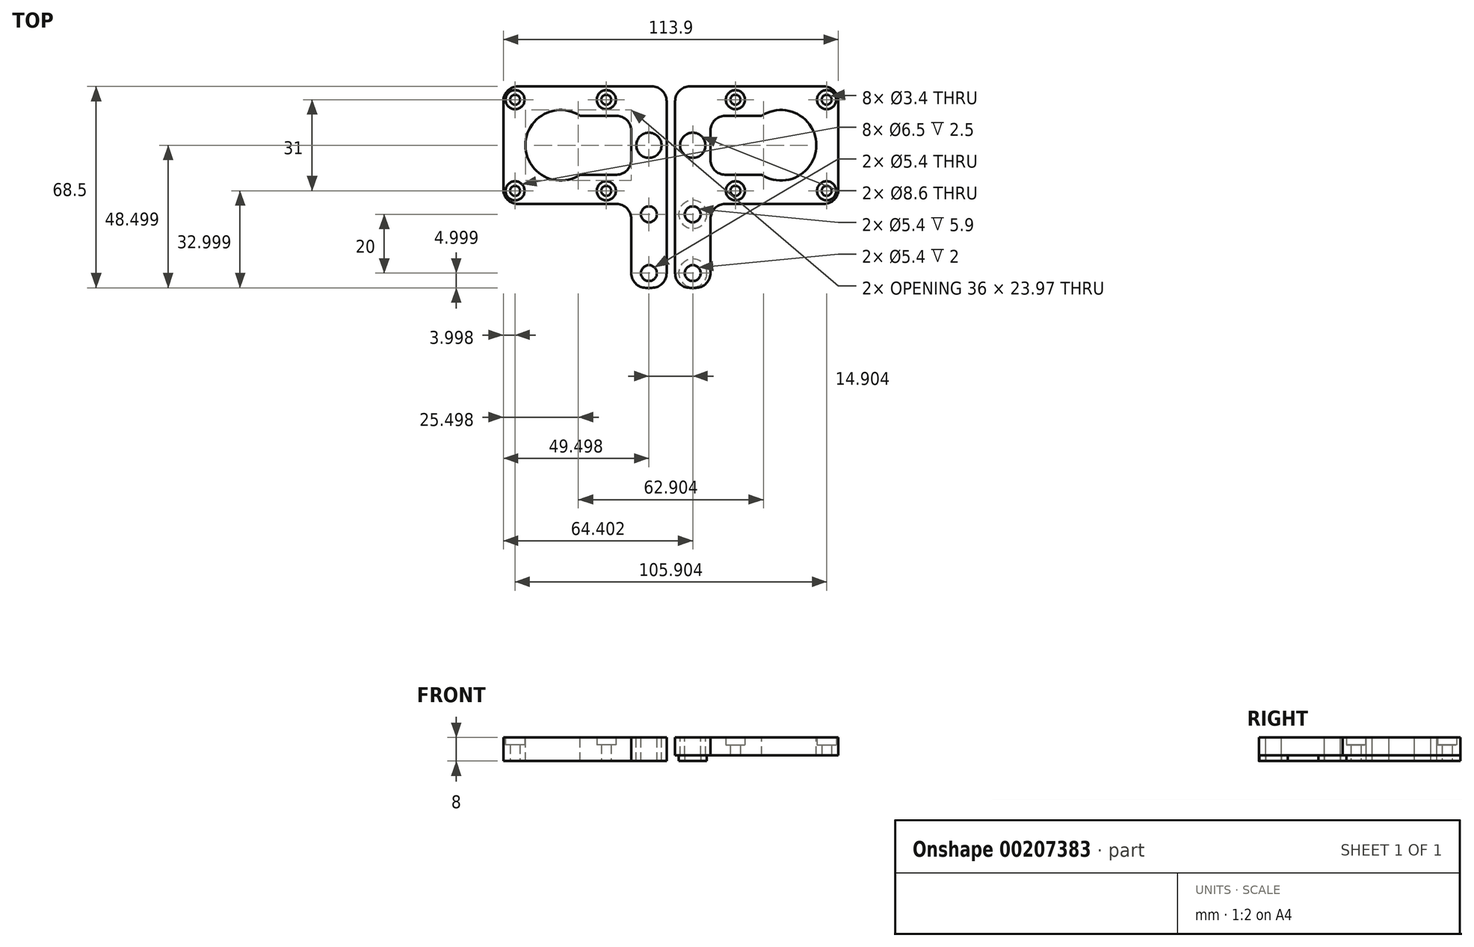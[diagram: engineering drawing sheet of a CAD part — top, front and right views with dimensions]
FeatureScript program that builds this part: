
annotation { "Feature Type Name" : "Feature", "Feature Type Description" : "" }
export const myFeature = defineFeature(function(context is Context, id is Id, definition is map)
    precondition{}
    {
        {
            var Q0;
            Q0=qCreatedBy(makeId("Top.planeOp"),FACE);
            var sketch = newSketch(context, id + "F0", { "sketchPlane" : qUnion([Q0])});
            skLineSegment(sketch, "E0.top", {"start": v(1.45, 0.9) * mm, "end": v(13.45, 0.9) * mm});
            skCircle(sketch, "E1", {"center": v(7.45, 49.4) * mm, "radius": 4.3 * mm});
            skCircle(sketch, "E2", {"center": v(7.45, 25.9) * mm, "radius": 2.7 * mm});
            skCircle(sketch, "E3", {"center": v(7.45, 5.9) * mm, "radius": 2.7 * mm});
            skPoint(sketch, "E4", {"position": v(7.45, 0.9) * mm});
            skLineSegment(sketch, "E5", {"start": v(56.95, 29.4) * mm, "end": v(56.95, 69.4) * mm});
            skLineSegment(sketch, "E6", {"start": v(13.45, 59.4) * mm, "end": v(48.95, 59.4) * mm});
            skLineSegment(sketch, "E7", {"start": v(21.95, 33.9) * mm, "end": v(52.95, 64.9) * mm, "construction": true});
            skLineSegment(sketch, "E8", {"start": v(52.95, 33.9) * mm, "end": v(21.95, 64.9) * mm, "construction": true});
            skPoint(sketch, "E9", {"position": v(37.45, 49.4) * mm});
            skLineSegment(sketch, "E10", {"start": v(13.45, 29.4) * mm, "end": v(56.95, 29.4) * mm});
            skLineSegment(sketch, "E11", {"start": v(13.45, 69.4) * mm, "end": v(56.95, 69.4) * mm});
            skLineSegment(sketch, "E12", {"start": v(13.45, 69.4) * mm, "end": v(1.45, 69.4) * mm});
            skLineSegment(sketch, "E13", {"start": v(48.95, 59.4) * mm, "end": v(48.95, 39.4) * mm});
            skLineSegment(sketch, "E14", {"start": v(48.95, 39.4) * mm, "end": v(13.45, 39.4) * mm});
            skLineSegment(sketch, "E15", {"start": v(13.45, 0.9) * mm, "end": v(13.45, 29.4) * mm});
            skLineSegment(sketch, "E16", {"start": v(1.45, 0.9) * mm, "end": v(1.45, 69.4) * mm});
            skLineSegment(sketch, "E17", {"start": v(13.45, 39.4) * mm, "end": v(13.45, 59.4) * mm});
            skCircle(sketch, "E18", {"center": v(37.45, 49.4) * mm, "radius": 12 * mm});
            skCircle(sketch, "E19", {"center": v(7.45, 5.9) * mm, "radius": 4.8 * mm});
            skCircle(sketch, "E20", {"center": v(7.45, 25.9) * mm, "radius": 4.8 * mm});
            skSolve(sketch);
        }
        {
            var Q0;
            Q0=makeQuery(id+"F0.imprint","IMPRINT",FACE,{"disambiguationData":[TD([[makeQuery(id+"F0.imprint","IMPRINT",EDGE,{"derivedFrom":sQuery(id+"F0.wireOp",EDGE,"E0.bottom")}),-1.0]])]});
            var Q1;
            {var subQ1=sQuery(id+"F0.wireOp",EDGE,"d5d79a18-1b9a-439a-83fc-479bf9618a3d");Q1=makeQuery(id+"F0.imprint","IMPRINT",FACE,{"disambiguationData":[TD([[makeQuery(id+"F0.imprint","IMPRINT",EDGE,{"derivedFrom":subQ1}),-1.0]])]});}
            var Q2;
            Q2=makeQuery(id+"F0.imprint","IMPRINT",FACE,{"disambiguationData":[TD([[makeQuery(id+"F0.imprint","IMPRINT",EDGE,{"derivedFrom":sQuery(id+"F0.wireOp",EDGE,"E0.bottom")}),1.0]])]});
            var Q3;
            {var subQ5=sQuery(id+"F0.wireOp",EDGE,"E0.top");Q3=makeQuery(id+"F0.imprint","IMPRINT",FACE,{"disambiguationData":[TD([[makeQuery(id+"F0.imprint","IMPRINT",EDGE,{"derivedFrom":subQ5}),1.0]])]});}
            var Q4;
            {var subQ4=sQuery(id+"F0.wireOp",EDGE,"c570f75a-df84-4235-972a-370a758feee2");Q4=makeQuery(id+"F0.imprint","IMPRINT",FACE,{"disambiguationData":[TD([[makeQuery(id+"F0.imprint","IMPRINT",EDGE,{"derivedFrom":subQ4}),-1.0]])]});}
            var Q5;
            Q5=makeQuery(id+"F0.imprint","IMPRINT",FACE,{"disambiguationData":[TD([[makeQuery(id+"F0.imprint","IMPRINT",EDGE,{"derivedFrom":sQuery(id+"F0.wireOp",EDGE,"E5")}),1.0]])]});
            var Q6;
            {var subQ0=sQuery(id+"F0.wireOp",EDGE,"E13");var subQ1=sQuery(id+"F0.wireOp",EDGE,"E6");var subQ2=makeQuery(id+"F0.imprint","INTERSECT",VERTEX,{"derivedFrom":[subQ1,subQ0]});Q6=makeQuery(id+"F0.imprint","IMPRINT",FACE,{"disambiguationData":[TD([[makeQuery(id+"F0.imprint","IMPRINT",EDGE,{"disambiguationData":[TD([[subQ2,1.0]])],"derivedFrom":subQ1}),-1.0]])]});}
            var Q7;
            {var subQ0=sQuery(id+"F0.wireOp",EDGE,"E14");var subQ1=sQuery(id+"F0.wireOp",EDGE,"E13");var subQ2=makeQuery(id+"F0.imprint","INTERSECT",VERTEX,{"derivedFrom":[subQ1,subQ0]});Q7=makeQuery(id+"F0.imprint","IMPRINT",FACE,{"disambiguationData":[TD([[makeQuery(id+"F0.imprint","IMPRINT",EDGE,{"disambiguationData":[TD([[subQ2,1.0]])],"derivedFrom":subQ1}),-1.0]])]});}
            var Q8;
            Q8=makeQuery(id+"F0.imprint","IMPRINT",FACE,{"disambiguationData":[TD([[makeQuery(id+"F0.imprint","IMPRINT",EDGE,{"derivedFrom":sQuery(id+"F0.wireOp",EDGE,"E3")}),-1.0]])]});
            var Q9;
            Q9=makeQuery(id+"F0.imprint","IMPRINT",FACE,{"disambiguationData":[TD([[makeQuery(id+"F0.imprint","IMPRINT",EDGE,{"derivedFrom":sQuery(id+"F0.wireOp",EDGE,"E2")}),-1.0]])]});
            extrude(context, id + "F1", {"entities" : qUnion([Q0, Q1, Q2, Q3, Q4, Q5, Q6, Q7, Q8, Q9]), "oppositeDirection" : true, "depth" : 8 * mm, "offsetDistance" : 25 * mm});
        }
        {
            var Q0;
            Q0=makeQuery(id+"F1.opExtrude","SWEPT_EDGE",EDGE,{"disambiguationData":[OSD([sQuery(id+"F0.wireOp",EDGE,"E5"),sQuery(id+"F0.wireOp",EDGE,"E10")])]});
            var Q1;
            Q1=makeQuery(id+"F1.opExtrude","SWEPT_EDGE",EDGE,{"disambiguationData":[OSD([sQuery(id+"F0.wireOp",EDGE,"E5"),sQuery(id+"F0.wireOp",EDGE,"E11")])]});
            var Q2;
            Q2=makeQuery(id+"F1.opExtrude","SWEPT_EDGE",EDGE,{"disambiguationData":[OSD([sQuery(id+"F0.wireOp",EDGE,"E12"),sQuery(id+"F0.wireOp",EDGE,"E16")])]});
            var Q3;
            Q3=makeQuery(id+"F1.opExtrude","SWEPT_EDGE",EDGE,{"disambiguationData":[OSD([sQuery(id+"F0.wireOp",EDGE,"E0.top"),sQuery(id+"F0.wireOp",EDGE,"E15")])]});
            var Q4;
            Q4=makeQuery(id+"F1.opExtrude","SWEPT_EDGE",EDGE,{"disambiguationData":[OSD([sQuery(id+"F0.wireOp",EDGE,"E0.top"),sQuery(id+"F0.wireOp",EDGE,"E16")])]});
            var Q5;
            Q5=makeQuery(id+"F1.opExtrude","SWEPT_EDGE",EDGE,{"disambiguationData":[OSD([sQuery(id+"F0.wireOp",EDGE,"E10"),sQuery(id+"F0.wireOp",EDGE,"E15")])]});
            var Q6;
            Q6=makeQuery(id+"F1.opExtrude","SWEPT_EDGE",EDGE,{"disambiguationData":[OSD([sQuery(id+"F0.wireOp",EDGE,"E6"),sQuery(id+"F0.wireOp",EDGE,"E17")])]});
            var Q7;
            Q7=makeQuery(id+"F1.opExtrude","SWEPT_EDGE",EDGE,{"disambiguationData":[OSD([sQuery(id+"F0.wireOp",EDGE,"E14"),sQuery(id+"F0.wireOp",EDGE,"E17")])]});
            fillet(context, id + "F2", {"entities" : qUnion([Q0, Q1, Q2, Q3, Q4, Q5, Q6, Q7]), "radius" : 5 * mm, "tangentPropagation" : true, "allowEdgeOverflow" : false});
        }
        {
            var Q0;
            Q0=sQuery(id+"F0.wireOp",VERTEX,"E8.end");
            var Q1;
            Q1=sQuery(id+"F0.wireOp",VERTEX,"E7.end");
            var Q2;
            Q2=sQuery(id+"F0.wireOp",VERTEX,"E8.start");
            var Q3;
            Q3=sQuery(id+"F0.wireOp",VERTEX,"E7.start");
            var Q4;
            Q4=makeQuery(id+"F1.opExtrude","SWEPT_BODY",BODY,{"disambiguationData":[OSD([sQuery(id+"F0.wireOp",EDGE,"E0.top"),sQuery(id+"F0.wireOp",EDGE,"E1"),sQuery(id+"F0.wireOp",EDGE,"E2"),sQuery(id+"F0.wireOp",EDGE,"E3"),sQuery(id+"F0.wireOp",EDGE,"E5"),sQuery(id+"F0.wireOp",EDGE,"E6"),sQuery(id+"F0.wireOp",EDGE,"E10"),sQuery(id+"F0.wireOp",EDGE,"E11"),sQuery(id+"F0.wireOp",EDGE,"E12"),sQuery(id+"F0.wireOp",EDGE,"E14"),sQuery(id+"F0.wireOp",EDGE,"E15"),sQuery(id+"F0.wireOp",EDGE,"E16"),sQuery(id+"F0.wireOp",EDGE,"E17"),sQuery(id+"F0.wireOp",EDGE,"E18")])]});
            hole(context, id + "F3", {"style" : HoleStyle.C_BORE, "endStyle" : HoleEndStyle.THROUGH, "holeDiameter" : 3.4 * mm, "cBoreDiameter" : 6.5 * mm, "cBoreDepth" : 2.5 * mm, "majorDiameter" : 5 * mm, "isTappedThrough" : true, "tappedDepth" : 12 * mm, "tapClearance" : 3, "locations" : qUnion([Q0, Q1, Q2, Q3]), "scope" : qUnion([Q4]), "startStyle" : HoleStartStyle.PART});
        }
        {
            var Q0;
            Q0=makeQuery(id+"F1.opExtrude","SWEPT_BODY",BODY,{"disambiguationData":[OSD([sQuery(id+"F0.wireOp",EDGE,"E0.top"),sQuery(id+"F0.wireOp",EDGE,"E0.left"),sQuery(id+"F0.wireOp",EDGE,"E0.right"),sQuery(id+"F0.wireOp",EDGE,"E1"),sQuery(id+"F0.wireOp",EDGE,"E2"),sQuery(id+"F0.wireOp",EDGE,"E3"),sQuery(id+"F0.wireOp",EDGE,"d5d79a18-1b9a-439a-83fc-479bf9618a3d"),sQuery(id+"F0.wireOp",EDGE,"c570f75a-df84-4235-972a-370a758feee2"),sQuery(id+"F0.wireOp",EDGE,"a2be1d45-0dba-40e6-a96d-5c1e5a46a9f0"),sQuery(id+"F0.wireOp",EDGE,"d066aa0a-05fd-4a1e-85b8-d3e250bc6735"),sQuery(id+"F0.wireOp",EDGE,"028c346d-4075-4f4f-a344-9214535dc93d"),sQuery(id+"F0.wireOp",EDGE,"923343ab-d8ea-4514-8808-893b9cc318f7"),sQuery(id+"F0.wireOp",EDGE,"97896662-81bd-4ab9-9ddb-92a6698ae74e"),sQuery(id+"F0.wireOp",EDGE,"62df8057-97cc-498b-857e-02ef16877537")])]});
            var Q1;
            Q1=qCreatedBy(makeId("Right.planeOp"),FACE);
            mirror(context, id + "F4", {"entities" : qUnion([Q0]), "mirrorPlane" : qUnion([Q1])});
        }
        {
            var Q0;
            Q0=makeQuery(id+"F1.opExtrude","CAP_FACE",FACE,{"disambiguationData":[OSD([sQuery(id+"F0.wireOp",EDGE,"E0.top"),sQuery(id+"F0.wireOp",EDGE,"E1"),sQuery(id+"F0.wireOp",EDGE,"E2"),sQuery(id+"F0.wireOp",EDGE,"E3"),sQuery(id+"F0.wireOp",EDGE,"E5"),sQuery(id+"F0.wireOp",EDGE,"E6"),sQuery(id+"F0.wireOp",EDGE,"E10"),sQuery(id+"F0.wireOp",EDGE,"E11"),sQuery(id+"F0.wireOp",EDGE,"E12"),sQuery(id+"F0.wireOp",EDGE,"E14"),sQuery(id+"F0.wireOp",EDGE,"E15"),sQuery(id+"F0.wireOp",EDGE,"E16"),sQuery(id+"F0.wireOp",EDGE,"E17"),sQuery(id+"F0.wireOp",EDGE,"E18")])],"isStart":false});
            var sketch = newSketch(context, id + "F5", { "sketchPlane" : qUnion([Q0])});
            skCircle(sketch, "E21.0", {"center": v(7.45, -5.9) * mm, "radius": 4.8 * mm});
            skCircle(sketch, "E22.0", {"center": v(7.45, -25.9) * mm, "radius": 4.8 * mm});
            skCircle(sketch, "E23.0", {"center": v(7.45, -5.9) * mm, "radius": 2.7 * mm});
            skSolve(sketch);
        }
        {
            var Q0;
            Q0=makeQuery(id+"F5.imprint","IMPRINT",FACE,{"disambiguationData":[TD([[makeQuery(id+"F5.imprint","IMPRINT",EDGE,{"derivedFrom":sQuery(id+"F5.wireOp",EDGE,"E21.0")}),-1.0]])]});
            var Q1;
            Q1=makeQuery(id+"F5.imprint","IMPRINT",FACE,{"disambiguationData":[TD([[makeQuery(id+"F5.imprint","IMPRINT",EDGE,{"derivedFrom":sQuery(id+"F5.wireOp",EDGE,"E23.0")}),-1.0]])]});
            var Q2;
            Q2=makeQuery(id+"F5.imprint","IMPRINT",FACE,{"disambiguationData":[TD([[makeQuery(id+"F5.imprint","IMPRINT",EDGE,{"derivedFrom":makeQuery(id+"F1.opExtrude","CAP_EDGE",EDGE,{"disambiguationData":[OSD([sQuery(id+"F0.wireOp",EDGE,"E2")])],"isStart":false})}),-1.0]])]});
            extrude(context, id + "F6", {"entities" : qUnion([Q0, Q1, Q2]), "operationType" : NewBodyOperationType.ADD, "oppositeDirection" : true, "depth" : 2.1 * mm, "offsetDistance" : 25 * mm});
        }
        {
            var Q0;
            Q0=makeQuery(id+"F5.imprint","IMPRINT",FACE,{"disambiguationData":[TD([[makeQuery(id+"F5.imprint","IMPRINT",EDGE,{"derivedFrom":sQuery(id+"F5.wireOp",EDGE,"E21.0")}),-1.0]])]});
            var Q1;
            Q1=makeQuery(id+"F5.imprint","IMPRINT",FACE,{"disambiguationData":[TD([[makeQuery(id+"F5.imprint","IMPRINT",EDGE,{"derivedFrom":sQuery(id+"F5.wireOp",EDGE,"E22.0")}),-1.0]])]});
            var Q2;
            Q2=makeQuery(id+"F5.imprint","IMPRINT",FACE,{"disambiguationData":[TD([[makeQuery(id+"F5.imprint","IMPRINT",EDGE,{"derivedFrom":sQuery(id+"F5.wireOp",EDGE,"E23.0")}),-1.0]])]});
            var Q3;
            Q3=makeQuery(id+"F5.imprint","IMPRINT",FACE,{"disambiguationData":[TD([[makeQuery(id+"F5.imprint","IMPRINT",EDGE,{"derivedFrom":makeQuery(id+"F1.opExtrude","CAP_EDGE",EDGE,{"disambiguationData":[OSD([sQuery(id+"F0.wireOp",EDGE,"E2")])],"isStart":false})}),-1.0]])]});
            var Q4;
            Q4=sQuery(id+"F5.wireOp",EDGE,"E21.0");
            extrude(context, id + "F7", {"entities" : qUnion([Q0, Q1, Q2, Q3]), "operationType" : NewBodyOperationType.REMOVE, "surfaceEntities" : qUnion([Q4]), "oppositeDirection" : true, "depth" : 2 * mm, "offsetDistance" : 25 * mm});
        }
    });
